# Revit family: C_ABR10525_2DO_Cad_MULT_Prod
name_source: partatom
category: Detail Items
revit_build: Autodesk Revit 2014 (Build: 20130308_1515(x64)
units: mm (PartAtom-declared; Revit-internal decimal feet)

## types (4) — shared parameters
Density = 0.34 kg
Description = Angle brackets
EPD = https://www.strongtie.eu
ETA / DoP = https://www.strongtie.eu
Manufacturer = Simpson Strong-Tie
Model = ABR10525
Model Disclaimer = Contact Simpson Strong-Tie Company  for more information
Model ID = 0097530612414003422649466609165937728177
Name = ABR10525
ObjectType = ABR10525
Product Material = Galvanised
Product Type = Angle brackets
Reference = ABR10525
Technical datasheet = https://www.strongtie.eu
URL = www.strongtie.eu
UniClass Number = Pr_20_85_09_09
UniClass Title = Bracketed angle supports

## per-type parameters (varying)
| type | _visiblefront | _visibleleft | _visibleright | _visibletop |
| SST_ABR10525_Front View | Yes | No | No | No |
| SST_ABR10525_Top View | No | No | No | Yes |
| SST_ABR10525_Left View | No | Yes | No | No |
| SST_ABR10525_Right View | No | No | Yes | No |

## geometry (parser evidence)
native form markers: Sweep x2
no freeform markers — native parametric forms only
